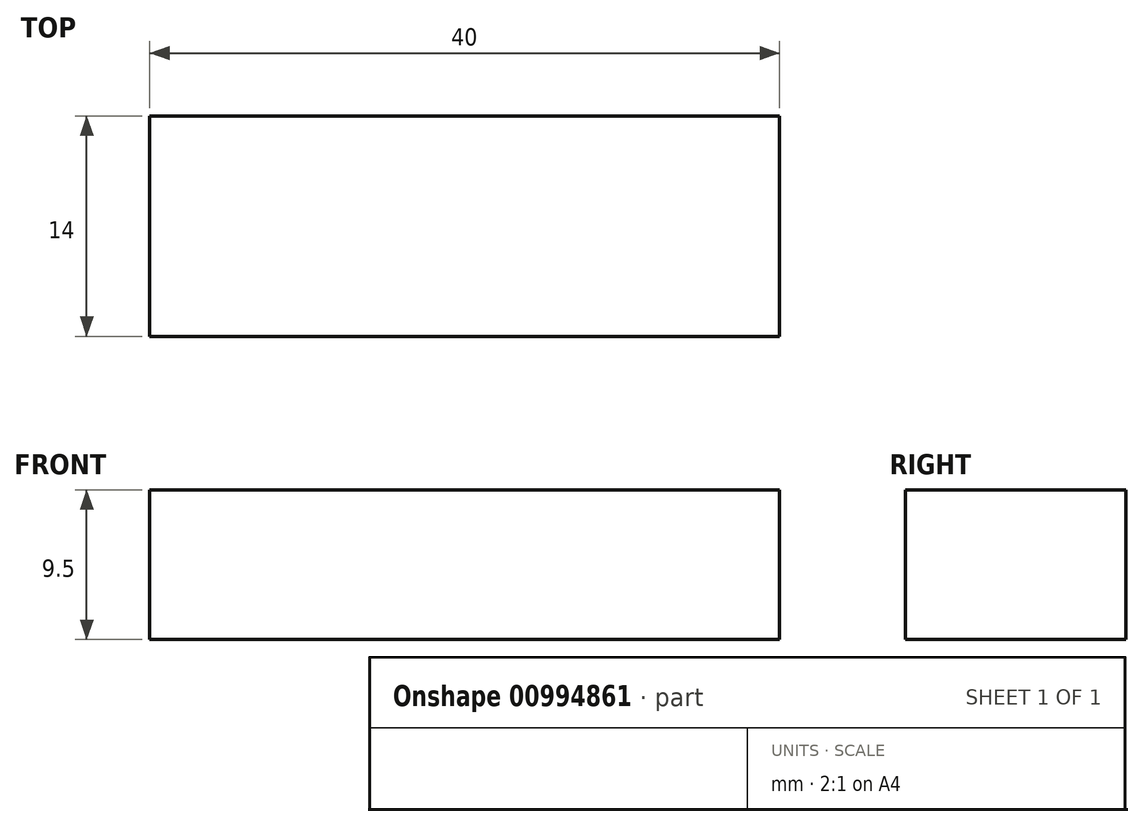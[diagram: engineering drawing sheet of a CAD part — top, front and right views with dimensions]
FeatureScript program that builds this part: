
annotation { "Feature Type Name" : "Feature", "Feature Type Description" : "" }
export const myFeature = defineFeature(function(context is Context, id is Id, definition is map)
    precondition{}
    {
        {
            var Q0;
            Q0=qCreatedBy(makeId("Top.planeOp"),FACE);
            var sketch = newSketch(context, id + "F0", { "sketchPlane" : qUnion([Q0])});
            skLineSegment(sketch, "E0.bottom", {"start": v(20, -7) * mm, "end": v(-20, -7) * mm});
            skLineSegment(sketch, "E0.top", {"start": v(20, 7) * mm, "end": v(-20, 7) * mm});
            skLineSegment(sketch, "E0.left", {"start": v(20, -7) * mm, "end": v(20, 7) * mm});
            skLineSegment(sketch, "E0.right", {"start": v(-20, -7) * mm, "end": v(-20, 7) * mm});
            skPoint(sketch, "E0.middle", {"position": v(0, 0) * mm});
            skSolve(sketch);
        }
        {
            var Q0;
            Q0 = qSketchRegion(id + "F0", true);
            extrude(context, id + "F1", {"entities" : qUnion([Q0]), "depth" : 9.5 * mm, "offsetDistance" : 25 * mm});
        }
    });
